# Revit family: Innovo BEFR_IR 32 245 BEFR LP
name_source: partatom
category: Mechanical Equipment
revit_build: Autodesk Revit 2015 (Build: 20160512_0715(x64)
units: mm (PartAtom-declared; Revit-internal decimal feet)

## types (1)
- IR-32-245 BEFR LP
    1er Entretien (check-up) = 3 mois après l'installation
    2ème Entretien (Entretien Général) = 12 mois après l'installation
    Annual electricity consumption (1) = 44 kWh
    Annual electricity consumption (2) = -
    Annual fuel consumption (1) = 21 GJ GCV
    Annual fuel consumption (2) = -
    Assembly Code = D3010
    BIM Content Developer = CAD & Company
    CE-PIN = 0063CQ3037
    CO2 Émissions (tol. +/- 1.0) vol% = 10.0
    Capacité = 245.0 L
    Catégorie de Gaz = I3P
    Charge Maximale au Sol = 381 kg
    Charge Nominale (Valeur Inférieure) = 29000.0
    Charge Nominale (Valeur Supérieure) = 31500.0
    Class d'efficacité énergétique (1) = A
    Class d'efficacité énergétique (2) = -
    Consommation de Gaz - Masse kg/h = 2.3
    Consommation de Gaz - Volume ltr/hr = a/p
    D'autres profils de soutirage = -
    Description = Préparateur ECS Solaire en Combinaison avec Réservoir de Stockage
    Destination / Country = Belgique
    Diameter = 610 mm  [stored 2.00131 ft]
    Diamètre Cheminée - Boiler = 80/125 mm/mm
    Diamètre Cheminée - Système Concentrique = 80/125 mm/mm
    Diamètre Cheminée - Système Parallèle = 2x80
    Débit de vidage en Continu à ΔT = 28°C = 960.0 L/s
    Débit de vidage en Continu à ΔT = 44°C = 600.0 L/s
    Débit de vidage en Continu à ΔT = 50°C = 530.0 L/s
    Débit de vidage en Continu à ΔT = 55°C = 480.0 L/s
    Débit de vidage en Continu à ΔT = 70°C = 380.0 L/s
    Débit de vidage à ΔT = 28°C après 120 min. = 2400.0 L
    Débit de vidage à ΔT = 28°C après 30 min. = 930.0 L
    Débit de vidage à ΔT = 28°C après 60 min. = 1400.0 L
    Débit de vidage à ΔT = 28°C après 90 min. = 1900.0 L
    Débit de vidage à ΔT = 44°C après 120 min. = 1500.0 L
    Débit de vidage à ΔT = 44°C après 30 min. = 570.0 L
    Débit de vidage à ΔT = 44°C après 60 min. = 870.0 L
    Débit de vidage à ΔT = 44°C après 90 min. = 1200.0 L
    Débit de vidage à ΔT = 50°C après 120 min. = 1300.0 L
    Débit de vidage à ΔT = 50°C après 30 min. = 500.0 L
    Débit de vidage à ΔT = 50°C après 60 min. = 760.0 L
    Débit de vidage à ΔT = 50°C après 90 min. = 1100.0 L
    Débit de vidage à ΔT = 55°C après 120 min. = 1200.0 L
    Débit de vidage à ΔT = 55°C après 30 min. = 440.0 L
    Débit de vidage à ΔT = 55°C après 60 min. = 690.0 L
    Débit de vidage à ΔT = 55°C après 90 min. = 930.0 L
    Débit de vidage à ΔT = 70°C après 120 min. = 900.0 L
    Débit de vidage à ΔT = 70°C après 30 min. = 330.0 L
    Débit de vidage à ΔT = 70°C après 60 min. = 520.0 L
    Débit de vidage à ΔT = 70°C après 90 min. = 710.0 L
    Epaisseur d'Isolation = 44 mm  [stored 0.144357 ft]
    Fabricant No. = E 7110
    Forctionner qu'en heures creuses = No
    Fréquence secteur = 50 Hz
    Garantie Pièces = 12 mois
    Garantie sur la Cuve = 36 mois
    Hauteur = 1545 mm
    Hauteur Conduit d'Alimentation en Air = 1345 mm
    Hauteur Conduit d'Évacuation des Fumées = 1345 mm
    Hauteur d'emballage = 1695 mm
    Hauteur de l'Alimentation en eau Froide = 170 mm  [stored 0.557743 ft]
    Hauteur de la Sortie d'eau Chaude = 1545 mm
    Hauteur du Raccordement au Gaz = 920 mm  [stored 3.01837 ft]
    L'efficacité énergétique pour le chauffage de l'eau (1) = 92%
    L'efficacité énergétique pour le chauffage de l'eau (2) = -
    La commande intelligente = No
    Largeur = 610 mm  [stored 2.00131 ft]
    Manufacturer = A.O. Smith Water Products Company b.v.
    Marque commerciale = A.O. Smith
    Model = IR-32-325 FR LP
    Modèdele = IR-32-245
    NOx-émissions (ven air, 0% O2) ppm = 23
    NOx-émissions mg/kWh = 37
    Niveau de puissance acoustique à l'intérieur = 58 dB
    Niveau du Son dB (A) = <45
    Nombre de modèle du produit (EAN) = 8717449286262
    Pertes en Veille = 0 W
    Pertes en Veille - tous les jours (24h) = 0 W
    Phase = 1
    Poids de Transport = 136 kg
    Poids à vide = 120 kg
    Precaustions during assembling, installation or maintenance = voir Manuel d'installation, d'emploi er d'entretien
    Pression Amont de Gaz = 3700 Pa
    Pression Différentielle d'Ouverture de l'Interrupteur de Pression < = 210.0 Pa
    Pression de Fonctionnement Maximale = 800000.0 Pa
    Production Nominale = 30100.0
    Profils de soutirage déclaré = XXL
    Profondeur = 780 mm  [stored 2.55906 ft]
    Profondeur d'emballage = 946 mm  [stored 3.10367 ft]
    Puissance Électrique Absorbée (nominal) = 85 W
    Puissance Électrique Absorbée (sommet) = 105 W
    Raccord Robinet de Vidange = 3/4"
    Raccord d'Alimentation en Eau Froide = 3/4"
    Raccord de Gaz = 15"
    Raccord de Sortie d'Eau Chaude = 1"
    Raccord de la Soupape de Vidange = 1"
    Raccord Évacuation de la Condensation = 40 mm  [stored 0.131234 ft]
    Rendement (Hi, acc. NEN-EN 89 - 1999) = 106
    Rendement (Hs, acc. NEN-EN 89 - 1999) = 95
    Rendement Saisonnier (Hs) = 95
    Réglage Standard Pour = G31
    Réglages du thermostat du chauffe-eau = 65 °C
    Temps de réchauffement à ΔT = 28°C = 13
    Temps de réchauffement à ΔT = 44°C = 20
    Temps de réchauffement à ΔT = 50°C = 22
    Temps de réchauffement à ΔT = 55°C = 24
    Temps de réchauffement à ΔT = 70°C = 31
    Température Maximale des Fumées = 65 °C
    Tension d'Alimentation (-15%, +10%) = 230 V
    Type d'Installation = B23/C13/C33/C43/C53/C63
    Type d'emballage = Carton et bois
    URL = www.aosmith.be
    Valeur Défaut du Thermostat de Régulation = 65 °C
    Valeur Manimale du Thermostat de Régulation = 40 °C
    Valeur Maximale du Thermostat de Régulation = 85 °C
    Valve Height 01 = 693 mm  [stored 2.27362 ft]
    Valve Height 02 = 1328 mm  [stored 4.35696 ft]
    Workspace Front Distance = 1000 mm  [stored 3.28084 ft]
    Workspace Height = 2545 mm
    Workspace Radius = 780 mm  [stored 2.55906 ft]
    l'Intervalle d'Entretien = 12 mois
    largeur d'emballage = 786 mm  [stored 2.57874 ft]

note: [stored X ft] marks values corroborated as IEEE doubles in the binary element streams (Revit-internal decimal feet)

## geometry (parser evidence)
native form markers: Blend x26, Sweep x21
no freeform markers — native parametric forms only
